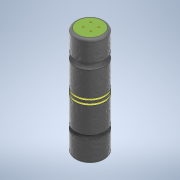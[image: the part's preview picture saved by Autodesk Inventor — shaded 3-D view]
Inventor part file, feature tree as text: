
AUTODESK INVENTOR PART (.ipt)
format: ipt  version: 2020 (Build 240168000, 168)  size: 203,264 bytes
history: native  units: mm
features: other x11, sketch x4, plane x3, revolve x2, extrude x1, fillet x1, projected_geometry x1
ambient origin geometry x8: Origin, YZ Plane, XZ Plane, XY Plane, X Axis, Y Axis, Z Axis, Center Point
bodies: Body1 (feature_tree)
feature tree (23):
  other  "Sólido1"
  extrude  "Extrusión1"  Depth=88.0mm TaperAngle=0.0deg
  plane  "Plano de trabajo1"
  plane  "Plano de trabajo2"
  sketch  "Boceto2"  dims[d3=0.0mm d4=1.5mm]
  other  "Eje de trabajo1"
  revolve  "Revolución1"  [1 undecoded]
  revolve  "Revolución2"  [1 undecoded]
  fillet  "Empalme1"  Radius=1.7mm
  sketch  "Boceto4"  dims[d8=0.0mm d9=90.0deg d10=5.0mm d11=25.0mm d12=5.0mm d13=25.0mm d14=90.0deg d15=2.0mm]
  other  "Eje de trabajo2"
  other  "+ext"
  other  "-ext"
  other  "Aext"
  other  "Bext"
  other  "+int"
  other  "-int"
  other  "Aint"
  other  "Bint"
  sketch  "Boceto1"  dims[d0=24.0mm d1=88.0mm d2=0.0mm]
  projected_geometry  "Contorno proyectado1"
  plane  "Plano de trabajo3"
  sketch  "Boceto3"  dims[d5=1.7mm d6=1.5mm d7=1.7mm]
note: 2 required parameter values undecoded (feature->parameter linkage not recoverable at this tier; creation-order binding heuristic only, values carry confidence <= 0.55)
